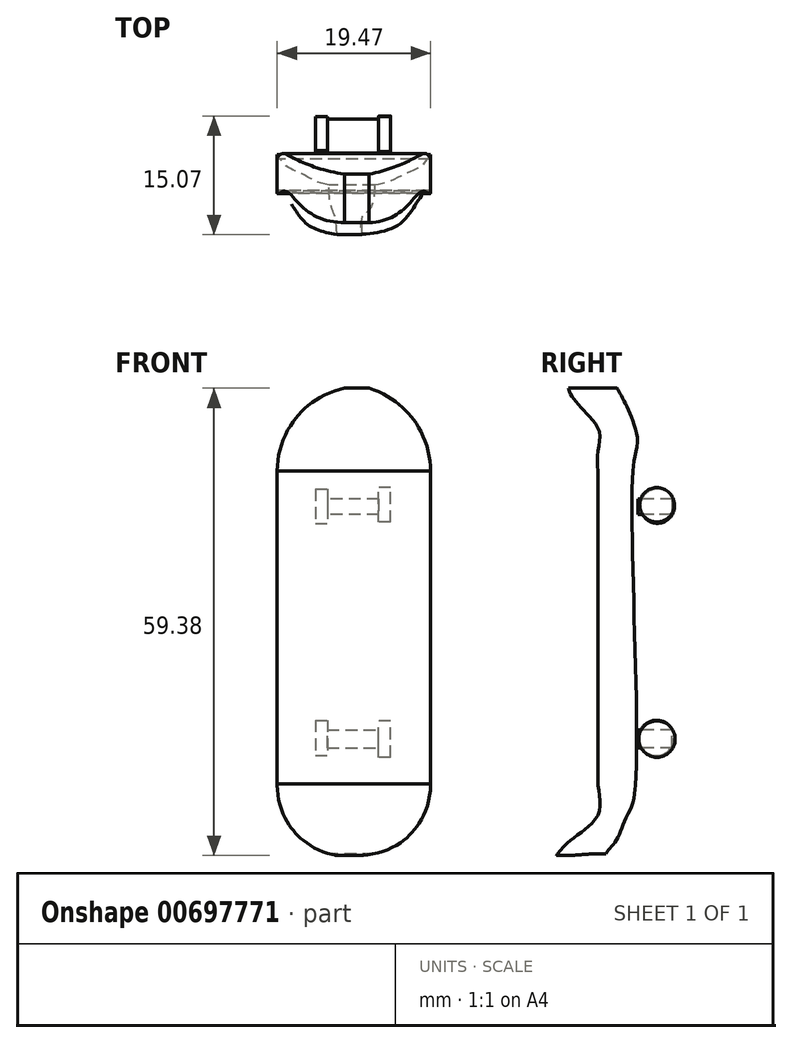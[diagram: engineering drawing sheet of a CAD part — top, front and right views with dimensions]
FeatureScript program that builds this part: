
annotation { "Feature Type Name" : "Feature", "Feature Type Description" : "" }
export const myFeature = defineFeature(function(context is Context, id is Id, definition is map)
    precondition{}
    {
        {
            var Q0;
            Q0=qCreatedBy(makeId("Front.planeOp"),FACE);
            var sketch = newSketch(context, id + "F0", { "sketchPlane" : qUnion([Q0])});
            skLineSegment(sketch, "E0.bottom", {"start": v(0, 0) * mm, "end": v(19.47, 0) * mm});
            skLineSegment(sketch, "E0.top", {"start": v(0, -39.9) * mm, "end": v(19.47, -39.9) * mm});
            skLineSegment(sketch, "E0.left", {"start": v(0, 0) * mm, "end": v(0, -39.9) * mm});
            skLineSegment(sketch, "E0.right", {"start": v(19.47, 0) * mm, "end": v(19.47, -39.9) * mm});
            skArc(sketch, "E1", {"start": v(10.8, 10.78) * mm, "mid": v(3.17, 7.63) * mm, "end": v(0, 0) * mm});
            skArc(sketch, "E2", {"start": v(19.47, 0) * mm, "mid": v(17.04, 6.92) * mm, "end": v(10.8, 10.78) * mm});
            skArc(sketch, "E3", {"start": v(0, -39.9) * mm, "mid": v(3.3, -46.9) * mm, "end": v(10.8, -48.78) * mm});
            skArc(sketch, "E4", {"start": v(10.8, -48.78) * mm, "mid": v(16.95, -46.1) * mm, "end": v(19.47, -39.9) * mm});
            skSolve(sketch);
        }
        {
            var Q0;
            Q0=makeQuery(id+"F0.imprint","IMPRINT",FACE,{"disambiguationData":[TD([[makeQuery(id+"F0.imprint","IMPRINT",EDGE,{"derivedFrom":sQuery(id+"F0.wireOp",EDGE,"E0.bottom")}),-1.0]])]});
            var Q1;
            Q1=makeQuery(id+"F0.imprint","IMPRINT",FACE,{"disambiguationData":[TD([[makeQuery(id+"F0.imprint","IMPRINT",EDGE,{"derivedFrom":sQuery(id+"F0.wireOp",EDGE,"E0.bottom")}),1.0]])]});
            var Q2;
            Q2=makeQuery(id+"F0.imprint","IMPRINT",FACE,{"disambiguationData":[TD([[makeQuery(id+"F0.imprint","IMPRINT",EDGE,{"derivedFrom":sQuery(id+"F0.wireOp",EDGE,"E0.top")}),-1.0]])]});
            extrude(context, id + "F1", {"entities" : qUnion([Q0, Q1, Q2]), "depth" : 53.85 * mm, "offsetDistance" : 25.4 * mm});
        }
        {
            var Q0;
            Q0=qCreatedBy(makeId("Right.planeOp"),FACE);
            cPlane(context, id + "F2", {"entities" : qUnion([Q0]), "cplaneType" : CPlaneType.OFFSET, "offset" : 49.02 * mm, "oppositeDirection" : true, "width" : 152.4 * mm, "height" : 152.4 * mm});
        }
        {
            var Q0;
            Q0=qCreatedBy(id+"F2.planeOp",FACE);
            var sketch = newSketch(context, id + "F3", { "sketchPlane" : qUnion([Q0])});
            skLineSegment(sketch, "E5", {"start": v(-36.86, 0) * mm, "end": v(-36.86, -39.72) * mm});
            skFitSpline(sketch, "E6", {"points": [v(-36.86, -39.72) * mm, v(-36.86, -43.72) * mm, v(-40.78, -47.28) * mm, v(-42.12, -48.83) * mm], "startDerivative": vector(1.29, -10.87) * mm, "endDerivative": vector(-4.83, -5.11) * mm});
            skFitSpline(sketch, "E7", {"points": [v(-36.86, 0) * mm, v(-36.86, 2.53) * mm, v(-36.86, 5.5) * mm, v(-40.6, 10.55) * mm], "startDerivative": vector(-0.37, 8.27) * mm, "endDerivative": vector(-2.47, 11.72) * mm});
            skLineSegment(sketch, "E8", {"start": v(-40.6, 10.55) * mm, "end": v(-34.45, 10.55) * mm});
            skFitSpline(sketch, "E9", {"points": [v(-34.45, 10.55) * mm, v(-32.44, 6.45) * mm, v(-31.82, 3.8) * mm, v(-32.4, 0) * mm, v(-32.2, -41.09) * mm, v(-33.32, -44.1) * mm, v(-34.45, -46.81) * mm, v(-35.82, -48.6) * mm], "startDerivative": vector(19.65, -30.48) * mm, "endDerivative": vector(-18.42, -28.09) * mm});
            skFitSpline(sketch, "E10", {"points": [v(-35.82, -48.6) * mm, v(-42.12, -48.83) * mm], "startDerivative": vector(-11.78, 0) * mm, "endDerivative": vector(-11.78, 0) * mm});
            skSolve(sketch);
        }
        {
            var Q0;
            Q0=makeQuery(id+"F3.imprint","IMPRINT",FACE,{"disambiguationData":[TD([[makeQuery(id+"F3.imprint","IMPRINT",EDGE,{"derivedFrom":sQuery(id+"F3.wireOp",EDGE,"E5")}),1.0]])]});
            extrude(context, id + "F4", {"entities" : qUnion([Q0]), "operationType" : NewBodyOperationType.INTERSECT, "depth" : 118.1 * mm, "offsetDistance" : 25.4 * mm});
        }
        {
            var Q0;
            Q0=qCreatedBy(makeId("Front.planeOp"),FACE);
            cPlane(context, id + "F5", {"entities" : qUnion([Q0]), "cplaneType" : CPlaneType.OFFSET, "offset" : 31.75 * mm, "width" : 152.4 * mm, "height" : 152.4 * mm});
        }
        {
            var Q0;
            Q0=qCreatedBy(id+"F5.planeOp",FACE);
            var sketch = newSketch(context, id + "F6", { "sketchPlane" : qUnion([Q0])});
            skLineSegment(sketch, "E11.bottom", {"start": v(6.39, -35.16) * mm, "end": v(12.9, -35.16) * mm});
            skLineSegment(sketch, "E11.top", {"start": v(6.39, -32.88) * mm, "end": v(12.9, -32.88) * mm});
            skLineSegment(sketch, "E11.left", {"start": v(6.39, -35.16) * mm, "end": v(6.39, -32.88) * mm});
            skLineSegment(sketch, "E11.right", {"start": v(12.9, -35.16) * mm, "end": v(12.9, -32.88) * mm});
            skLineSegment(sketch, "E12.bottom", {"start": v(12.9, -3.55) * mm, "end": v(6.39, -3.55) * mm});
            skLineSegment(sketch, "E12.top", {"start": v(12.9, -5.5) * mm, "end": v(6.39, -5.5) * mm});
            skLineSegment(sketch, "E12.left", {"start": v(12.9, -3.55) * mm, "end": v(12.9, -5.5) * mm});
            skLineSegment(sketch, "E12.right", {"start": v(6.39, -3.55) * mm, "end": v(6.39, -5.5) * mm});
            skSolve(sketch);
        }
        {
            var Q0;
            Q0=makeQuery(id+"F6.imprint","IMPRINT",FACE,{"disambiguationData":[TD([[makeQuery(id+"F6.imprint","IMPRINT",EDGE,{"derivedFrom":sQuery(id+"F6.wireOp",EDGE,"E12.bottom")}),1.0]])]});
            var Q1;
            Q1=makeQuery(id+"F6.imprint","IMPRINT",FACE,{"disambiguationData":[TD([[makeQuery(id+"F6.imprint","IMPRINT",EDGE,{"derivedFrom":sQuery(id+"F6.wireOp",EDGE,"E11.bottom")}),1.0]])]});
            extrude(context, id + "F7", {"entities" : qUnion([Q0, Q1]), "operationType" : NewBodyOperationType.ADD, "oppositeDirection" : true, "depth" : 4.32 * mm, "offsetDistance" : 25.4 * mm});
        }
        {
            var Q0;
            Q0=makeQuery(id+"F7.opExtrude","SWEPT_FACE",FACE,{"disambiguationData":[OSD([sQuery(id+"F6.wireOp",EDGE,"E12.left")])]});
            cPlane(context, id + "F8", {"entities" : qUnion([Q0]), "cplaneType" : CPlaneType.OFFSET, "offset" : 0 * mm, "oppositeDirection" : true, "width" : 152.4 * mm, "height" : 152.4 * mm});
        }
        {
            var Q0;
            Q0=qCreatedBy(id+"F8.planeOp",FACE);
            var sketch = newSketch(context, id + "F9", { "sketchPlane" : qUnion([Q0])});
            skCircle(sketch, "E13", {"center": v(-29.35, -4.28) * mm, "radius": 2.2 * mm});
            skCircle(sketch, "E14", {"center": v(-29.35, -34.04) * mm, "radius": 2.3 * mm});
            skSolve(sketch);
        }
        {
            var Q0;
            Q0=makeQuery(id+"F9.imprint","IMPRINT",FACE,{"disambiguationData":[TD([[makeQuery(id+"F9.imprint","IMPRINT",EDGE,{"derivedFrom":sQuery(id+"F9.wireOp",EDGE,"E13")}),1.0]])]});
            var Q1;
            Q1=makeQuery(id+"F9.imprint","IMPRINT",FACE,{"disambiguationData":[TD([[makeQuery(id+"F9.imprint","IMPRINT",EDGE,{"derivedFrom":sQuery(id+"F9.wireOp",EDGE,"E14")}),1.0]])]});
            extrude(context, id + "F10", {"entities" : qUnion([Q0, Q1]), "depth" : 1.52 * mm, "offsetDistance" : 25.4 * mm});
        }
        {
            var Q0;
            Q0=makeQuery(id+"F7.opExtrude","SWEPT_FACE",FACE,{"disambiguationData":[OSD([sQuery(id+"F6.wireOp",EDGE,"E12.right")])]});
            cPlane(context, id + "F11", {"entities" : qUnion([Q0]), "cplaneType" : CPlaneType.OFFSET, "offset" : 0 * mm, "width" : 152.4 * mm, "height" : 152.4 * mm});
        }
        {
            var Q0;
            Q0=qCreatedBy(id+"F11.planeOp",FACE);
            var sketch = newSketch(context, id + "F12", { "sketchPlane" : qUnion([Q0])});
            skCircle(sketch, "E15", {"center": v(29.29, -4.44) * mm, "radius": 2.18 * mm});
            skCircle(sketch, "E16", {"center": v(29.4, -33.89) * mm, "radius": 2.24 * mm});
            skSolve(sketch);
        }
        {
            var Q0;
            Q0=makeQuery(id+"F12.imprint","IMPRINT",FACE,{"disambiguationData":[TD([[makeQuery(id+"F12.imprint","IMPRINT",EDGE,{"derivedFrom":sQuery(id+"F12.wireOp",EDGE,"E16")}),1.0]])]});
            var Q1;
            Q1=makeQuery(id+"F12.imprint","IMPRINT",FACE,{"disambiguationData":[TD([[makeQuery(id+"F12.imprint","IMPRINT",EDGE,{"derivedFrom":sQuery(id+"F12.wireOp",EDGE,"E15")}),1.0]])]});
            extrude(context, id + "F13", {"entities" : qUnion([Q0, Q1]), "depth" : 1.52 * mm, "offsetDistance" : 25.4 * mm});
        }
    });
